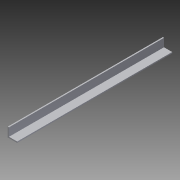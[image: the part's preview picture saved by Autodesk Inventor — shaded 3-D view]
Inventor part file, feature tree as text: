
AUTODESK INVENTOR PART (.ipt)
format: ipt  version: 2013 (Build 170138000, 138)  size: 71,680 bytes
history: native  units: in
note: dims shown in document units (in); Inventor stores cm internally (conversion verified against a paired STEP export)
features: extrude x1, sketch x1
ambient origin geometry x8: Origin, YZ Plane, XZ Plane, XY Plane, X Axis, Y Axis, Z Axis, Center Point
bodies: Solid1 (feature_tree)
feature tree (2):
  extrude  "Extrusion1"  Depth=0.0625in
  sketch  "Sketch1"  dims[d0=0.5in d1=0.0625in d2=0.5in d3=0.0625in d4=8.25in d5=0.0in]
